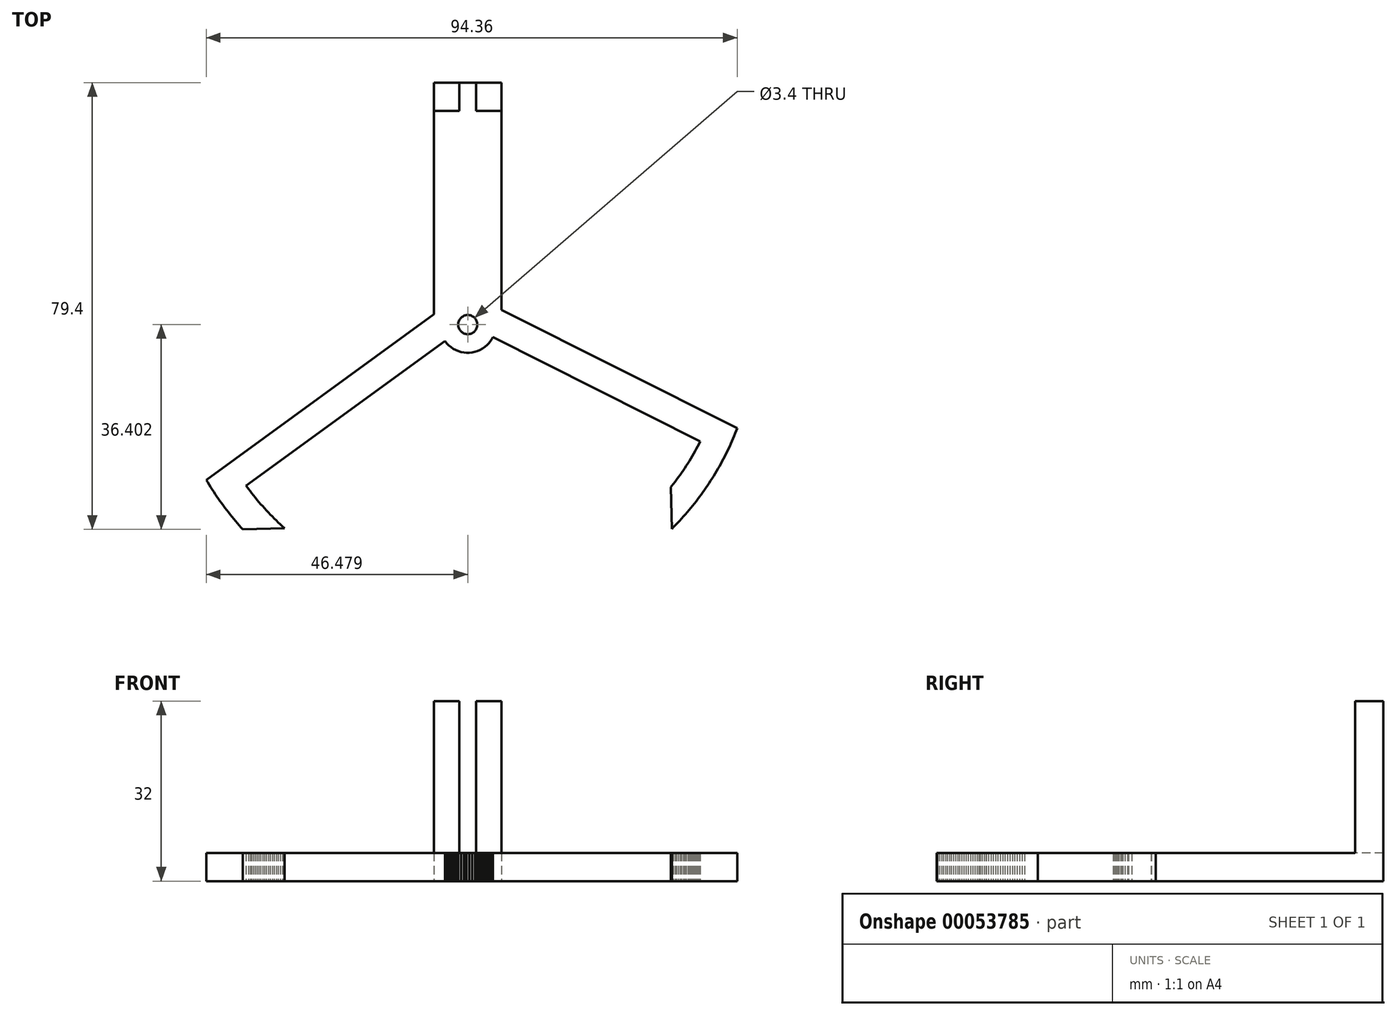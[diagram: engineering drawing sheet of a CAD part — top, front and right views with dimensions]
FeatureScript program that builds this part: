
annotation { "Feature Type Name" : "Feature", "Feature Type Description" : "" }
export const myFeature = defineFeature(function(context is Context, id is Id, definition is map)
    precondition{}
    {
        {
            var Q0;
            Q0=qCreatedBy(makeId("Top.planeOp"),FACE);
            var sketch = newSketch(context, id + "F0", { "sketchPlane" : qUnion([Q0])});
            skPoint(sketch, "E0", {"position": v(-0.7, 15.7) * mm});
            skLineSegment(sketch, "E1", {"start": v(0.8, 58.7) * mm, "end": v(0.8, 53.7) * mm});
            skLineSegment(sketch, "E2", {"start": v(-2.2, 58.7) * mm, "end": v(-2.2, 53.7) * mm});
            skLineSegment(sketch, "E3", {"start": v(-6.7, 58.7) * mm, "end": v(5.3, 58.7) * mm});
            skLineSegment(sketch, "E4", {"start": v(-6.7, 14.7) * mm, "end": v(-6.7, 58.7) * mm});
            skLineSegment(sketch, "E5", {"start": v(5.3, 14.7) * mm, "end": v(5.3, 58.7) * mm});
            skLineSegment(sketch, "E6", {"start": v(-6.7, 15.7) * mm, "end": v(5.3, 15.7) * mm, "construction": true});
            skLineSegment(sketch, "E7", {"start": v(-6.7, 14.7) * mm, "end": v(5.3, 14.7) * mm});
            skLineSegment(sketch, "E8", {"start": v(-6.7, 53.7) * mm, "end": v(5.3, 53.7) * mm});
            skLineSegment(sketch, "E9", {"start": v(-0.7, 14.7) * mm, "end": v(-0.7, 58.7) * mm, "construction": true});
            skCircle(sketch, "E10", {"center": v(-0.7, 15.7) * mm, "radius": 1.7 * mm});
            skPoint(sketch, "E9.startSnap0", {"position": v(-0.7, 14.7) * mm});
            skLineSegment(sketch, "E11", {"start": v(-33.28, -20.48) * mm, "end": v(-33.65, -20.15) * mm});
            skLineSegment(sketch, "E12", {"start": v(-33.65, -20.15) * mm, "end": v(-34.02, -19.8) * mm});
            skLineSegment(sketch, "E13", {"start": v(-34.02, -19.8) * mm, "end": v(-34.38, -19.46) * mm});
            skLineSegment(sketch, "E14", {"start": v(-34.38, -19.46) * mm, "end": v(-34.74, -19.11) * mm});
            skLineSegment(sketch, "E15", {"start": v(-34.74, -19.11) * mm, "end": v(-35.1, -18.76) * mm});
            skLineSegment(sketch, "E16", {"start": v(-35.1, -18.76) * mm, "end": v(-35.45, -18.4) * mm});
            skLineSegment(sketch, "E17", {"start": v(-35.45, -18.4) * mm, "end": v(-35.8, -18.05) * mm});
            skLineSegment(sketch, "E18", {"start": v(-35.8, -18.05) * mm, "end": v(-36.14, -17.69) * mm});
            skLineSegment(sketch, "E19", {"start": v(-36.14, -17.69) * mm, "end": v(-36.48, -17.32) * mm});
            skLineSegment(sketch, "E20", {"start": v(-36.48, -17.32) * mm, "end": v(-36.82, -16.95) * mm});
            skLineSegment(sketch, "E21", {"start": v(-36.82, -16.95) * mm, "end": v(-37.15, -16.58) * mm});
            skLineSegment(sketch, "E22", {"start": v(-37.15, -16.58) * mm, "end": v(-37.48, -16.2) * mm});
            skLineSegment(sketch, "E23", {"start": v(-37.48, -16.2) * mm, "end": v(-37.8, -15.82) * mm});
            skLineSegment(sketch, "E24", {"start": v(-37.8, -15.82) * mm, "end": v(-38.13, -15.44) * mm});
            skLineSegment(sketch, "E25", {"start": v(-38.13, -15.44) * mm, "end": v(-38.45, -15.06) * mm});
            skLineSegment(sketch, "E26", {"start": v(-38.45, -15.06) * mm, "end": v(-38.76, -14.67) * mm});
            skLineSegment(sketch, "E27", {"start": v(-38.76, -14.67) * mm, "end": v(-39.07, -14.27) * mm});
            skLineSegment(sketch, "E28", {"start": v(-39.07, -14.27) * mm, "end": v(-39.38, -13.88) * mm});
            skLineSegment(sketch, "E29", {"start": v(-39.38, -13.88) * mm, "end": v(-39.68, -13.48) * mm});
            skLineSegment(sketch, "E30", {"start": v(-39.68, -13.48) * mm, "end": v(-39.98, -13.08) * mm});
            skLineSegment(sketch, "E31", {"start": v(-39.98, -13.08) * mm, "end": v(-40.1, -12.92) * mm});
            skLineSegment(sketch, "E32", {"start": v(-40.1, -12.92) * mm, "end": v(-4.75, 12.76) * mm});
            skLineSegment(sketch, "E33", {"start": v(-4.75, 12.76) * mm, "end": v(-4.43, 12.37) * mm});
            skLineSegment(sketch, "E34", {"start": v(-4.43, 12.37) * mm, "end": v(-4.08, 12.02) * mm});
            skLineSegment(sketch, "E35", {"start": v(-4.08, 12.02) * mm, "end": v(-3.7, 11.7) * mm});
            skLineSegment(sketch, "E36", {"start": v(-3.7, 11.7) * mm, "end": v(-3.28, 11.42) * mm});
            skLineSegment(sketch, "E37", {"start": v(-3.28, 11.42) * mm, "end": v(-2.84, 11.18) * mm});
            skLineSegment(sketch, "E38", {"start": v(-2.84, 11.18) * mm, "end": v(-2.38, 11) * mm});
            skLineSegment(sketch, "E39", {"start": v(-2.38, 11) * mm, "end": v(-1.9, 10.85) * mm});
            skLineSegment(sketch, "E40", {"start": v(-1.9, 10.85) * mm, "end": v(-1.41, 10.75) * mm});
            skLineSegment(sketch, "E41", {"start": v(-1.41, 10.75) * mm, "end": v(-0.91, 10.7) * mm});
            skLineSegment(sketch, "E42", {"start": v(-0.91, 10.7) * mm, "end": v(-0.41, 10.71) * mm});
            skLineSegment(sketch, "E43", {"start": v(-0.41, 10.71) * mm, "end": v(0.08, 10.76) * mm});
            skLineSegment(sketch, "E44", {"start": v(0.08, 10.76) * mm, "end": v(0.57, 10.87) * mm});
            skLineSegment(sketch, "E45", {"start": v(0.57, 10.87) * mm, "end": v(1.05, 11.02) * mm});
            skLineSegment(sketch, "E46", {"start": v(1.05, 11.02) * mm, "end": v(1.5, 11.22) * mm});
            skLineSegment(sketch, "E47", {"start": v(1.5, 11.22) * mm, "end": v(1.94, 11.46) * mm});
            skLineSegment(sketch, "E48", {"start": v(1.94, 11.46) * mm, "end": v(2.35, 11.74) * mm});
            skLineSegment(sketch, "E49", {"start": v(2.35, 11.74) * mm, "end": v(2.73, 12.07) * mm});
            skLineSegment(sketch, "E50", {"start": v(2.73, 12.07) * mm, "end": v(3.08, 12.43) * mm});
            skLineSegment(sketch, "E51", {"start": v(3.08, 12.43) * mm, "end": v(3.39, 12.82) * mm});
            skLineSegment(sketch, "E52", {"start": v(3.39, 12.82) * mm, "end": v(3.65, 13.25) * mm});
            skLineSegment(sketch, "E53", {"start": v(3.65, 13.25) * mm, "end": v(3.77, 13.46) * mm});
            skLineSegment(sketch, "E54", {"start": v(3.77, 13.46) * mm, "end": v(40.61, -5.03) * mm});
            skLineSegment(sketch, "E55", {"start": v(40.61, -5.03) * mm, "end": v(40.39, -5.48) * mm});
            skLineSegment(sketch, "E56", {"start": v(40.39, -5.48) * mm, "end": v(40.15, -5.92) * mm});
            skLineSegment(sketch, "E57", {"start": v(40.15, -5.92) * mm, "end": v(39.92, -6.36) * mm});
            skLineSegment(sketch, "E58", {"start": v(39.92, -6.36) * mm, "end": v(39.68, -6.8) * mm});
            skLineSegment(sketch, "E59", {"start": v(39.68, -6.8) * mm, "end": v(39.43, -7.23) * mm});
            skLineSegment(sketch, "E60", {"start": v(39.43, -7.23) * mm, "end": v(39.18, -7.67) * mm});
            skLineSegment(sketch, "E61", {"start": v(39.18, -7.67) * mm, "end": v(38.93, -8.1) * mm});
            skLineSegment(sketch, "E62", {"start": v(38.93, -8.1) * mm, "end": v(38.67, -8.52) * mm});
            skLineSegment(sketch, "E63", {"start": v(38.67, -8.52) * mm, "end": v(38.4, -8.95) * mm});
            skLineSegment(sketch, "E64", {"start": v(38.4, -8.95) * mm, "end": v(38.13, -9.37) * mm});
            skLineSegment(sketch, "E65", {"start": v(38.13, -9.37) * mm, "end": v(37.86, -9.79) * mm});
            skLineSegment(sketch, "E66", {"start": v(37.86, -9.79) * mm, "end": v(37.58, -10.2) * mm});
            skLineSegment(sketch, "E67", {"start": v(37.58, -10.2) * mm, "end": v(37.3, -10.62) * mm});
            skLineSegment(sketch, "E68", {"start": v(37.3, -10.62) * mm, "end": v(37.01, -11.03) * mm});
            skLineSegment(sketch, "E69", {"start": v(37.01, -11.03) * mm, "end": v(36.72, -11.43) * mm});
            skLineSegment(sketch, "E70", {"start": v(36.72, -11.43) * mm, "end": v(36.42, -11.83) * mm});
            skLineSegment(sketch, "E71", {"start": v(36.42, -11.83) * mm, "end": v(36.12, -12.23) * mm});
            skLineSegment(sketch, "E72", {"start": v(36.12, -12.23) * mm, "end": v(35.82, -12.63) * mm});
            skLineSegment(sketch, "E73", {"start": v(35.82, -12.63) * mm, "end": v(35.51, -13.02) * mm});
            skLineSegment(sketch, "E74", {"start": v(35.51, -13.02) * mm, "end": v(35.4, -13.17) * mm});
            skLineSegment(sketch, "E75", {"start": v(35.4, -13.17) * mm, "end": v(35.57, -20.6) * mm});
            skLineSegment(sketch, "E76", {"start": v(35.57, -20.6) * mm, "end": v(35.92, -20.24) * mm});
            skLineSegment(sketch, "E77", {"start": v(35.92, -20.24) * mm, "end": v(36.27, -19.88) * mm});
            skLineSegment(sketch, "E78", {"start": v(36.27, -19.88) * mm, "end": v(36.61, -19.52) * mm});
            skLineSegment(sketch, "E79", {"start": v(36.61, -19.52) * mm, "end": v(36.95, -19.15) * mm});
            skLineSegment(sketch, "E80", {"start": v(36.95, -19.15) * mm, "end": v(37.3, -18.78) * mm});
            skLineSegment(sketch, "E81", {"start": v(37.3, -18.78) * mm, "end": v(37.63, -18.4) * mm});
            skLineSegment(sketch, "E82", {"start": v(37.63, -18.4) * mm, "end": v(37.96, -18.03) * mm});
            skLineSegment(sketch, "E83", {"start": v(37.96, -18.03) * mm, "end": v(38.28, -17.66) * mm});
            skLineSegment(sketch, "E84", {"start": v(38.28, -17.66) * mm, "end": v(38.6, -17.27) * mm});
            skLineSegment(sketch, "E85", {"start": v(38.6, -17.27) * mm, "end": v(38.93, -16.89) * mm});
            skLineSegment(sketch, "E86", {"start": v(38.93, -16.89) * mm, "end": v(39.24, -16.5) * mm});
            skLineSegment(sketch, "E87", {"start": v(39.24, -16.5) * mm, "end": v(39.55, -16.11) * mm});
            skLineSegment(sketch, "E88", {"start": v(39.55, -16.11) * mm, "end": v(39.86, -15.72) * mm});
            skLineSegment(sketch, "E89", {"start": v(39.86, -15.72) * mm, "end": v(40.17, -15.32) * mm});
            skLineSegment(sketch, "E90", {"start": v(40.17, -15.32) * mm, "end": v(40.47, -14.92) * mm});
            skLineSegment(sketch, "E91", {"start": v(40.47, -14.92) * mm, "end": v(40.76, -14.52) * mm});
            skLineSegment(sketch, "E92", {"start": v(40.76, -14.52) * mm, "end": v(41.06, -14.11) * mm});
            skLineSegment(sketch, "E93", {"start": v(41.06, -14.11) * mm, "end": v(41.34, -13.7) * mm});
            skLineSegment(sketch, "E94", {"start": v(41.34, -13.7) * mm, "end": v(41.63, -13.3) * mm});
            skLineSegment(sketch, "E95", {"start": v(41.63, -13.3) * mm, "end": v(41.9, -12.88) * mm});
            skLineSegment(sketch, "E96", {"start": v(41.9, -12.88) * mm, "end": v(42.19, -12.46) * mm});
            skLineSegment(sketch, "E97", {"start": v(42.19, -12.46) * mm, "end": v(42.46, -12.04) * mm});
            skLineSegment(sketch, "E98", {"start": v(42.46, -12.04) * mm, "end": v(42.73, -11.62) * mm});
            skLineSegment(sketch, "E99", {"start": v(42.73, -11.62) * mm, "end": v(43, -11.2) * mm});
            skLineSegment(sketch, "E100", {"start": v(43, -11.2) * mm, "end": v(43.25, -10.77) * mm});
            skLineSegment(sketch, "E101", {"start": v(43.25, -10.77) * mm, "end": v(43.5, -10.34) * mm});
            skLineSegment(sketch, "E102", {"start": v(43.5, -10.34) * mm, "end": v(43.76, -9.9) * mm});
            skLineSegment(sketch, "E103", {"start": v(43.76, -9.9) * mm, "end": v(44, -9.47) * mm});
            skLineSegment(sketch, "E104", {"start": v(44, -9.47) * mm, "end": v(44.25, -9.04) * mm});
            skLineSegment(sketch, "E105", {"start": v(44.25, -9.04) * mm, "end": v(44.49, -8.6) * mm});
            skLineSegment(sketch, "E106", {"start": v(44.49, -8.6) * mm, "end": v(44.72, -8.16) * mm});
            skLineSegment(sketch, "E107", {"start": v(44.72, -8.16) * mm, "end": v(44.95, -7.71) * mm});
            skLineSegment(sketch, "E108", {"start": v(44.95, -7.71) * mm, "end": v(45.18, -7.27) * mm});
            skLineSegment(sketch, "E109", {"start": v(45.18, -7.27) * mm, "end": v(45.4, -6.82) * mm});
            skLineSegment(sketch, "E110", {"start": v(45.4, -6.82) * mm, "end": v(45.62, -6.37) * mm});
            skLineSegment(sketch, "E111", {"start": v(45.62, -6.37) * mm, "end": v(45.83, -5.92) * mm});
            skLineSegment(sketch, "E112", {"start": v(45.83, -5.92) * mm, "end": v(46.04, -5.46) * mm});
            skLineSegment(sketch, "E113", {"start": v(46.04, -5.46) * mm, "end": v(46.24, -5) * mm});
            skLineSegment(sketch, "E114", {"start": v(46.24, -5) * mm, "end": v(46.44, -4.55) * mm});
            skLineSegment(sketch, "E115", {"start": v(46.44, -4.55) * mm, "end": v(46.64, -4.09) * mm});
            skLineSegment(sketch, "E116", {"start": v(46.64, -4.09) * mm, "end": v(46.83, -3.62) * mm});
            skLineSegment(sketch, "E117", {"start": v(46.83, -3.62) * mm, "end": v(47.01, -3.16) * mm});
            skLineSegment(sketch, "E118", {"start": v(47.01, -3.16) * mm, "end": v(47.18, -2.73) * mm});
            skLineSegment(sketch, "E119", {"start": v(47.18, -2.73) * mm, "end": v(1.54, 20.17) * mm});
            skLineSegment(sketch, "E120", {"start": v(1.54, 20.17) * mm, "end": v(1.08, 20.37) * mm});
            skLineSegment(sketch, "E121", {"start": v(1.08, 20.37) * mm, "end": v(0.6, 20.53) * mm});
            skLineSegment(sketch, "E122", {"start": v(0.6, 20.53) * mm, "end": v(0.12, 20.63) * mm});
            skLineSegment(sketch, "E123", {"start": v(0.12, 20.63) * mm, "end": v(-0.38, 20.7) * mm});
            skLineSegment(sketch, "E124", {"start": v(-0.38, 20.7) * mm, "end": v(-0.88, 20.7) * mm});
            skLineSegment(sketch, "E125", {"start": v(-0.88, 20.7) * mm, "end": v(-1.37, 20.66) * mm});
            skLineSegment(sketch, "E126", {"start": v(-1.37, 20.66) * mm, "end": v(-1.87, 20.56) * mm});
            skLineSegment(sketch, "E127", {"start": v(-1.87, 20.56) * mm, "end": v(-2.34, 20.42) * mm});
            skLineSegment(sketch, "E128", {"start": v(-2.34, 20.42) * mm, "end": v(-2.8, 20.24) * mm});
            skLineSegment(sketch, "E129", {"start": v(-2.8, 20.24) * mm, "end": v(-3.25, 20) * mm});
            skLineSegment(sketch, "E130", {"start": v(-3.25, 20) * mm, "end": v(-3.64, 19.75) * mm});
            skLineSegment(sketch, "E131", {"start": v(-3.64, 19.75) * mm, "end": v(-47.18, -11.89) * mm});
            skLineSegment(sketch, "E132", {"start": v(-47.18, -11.89) * mm, "end": v(-46.92, -12.32) * mm});
            skLineSegment(sketch, "E133", {"start": v(-46.92, -12.32) * mm, "end": v(-46.66, -12.74) * mm});
            skLineSegment(sketch, "E134", {"start": v(-46.66, -12.74) * mm, "end": v(-46.4, -13.17) * mm});
            skLineSegment(sketch, "E135", {"start": v(-46.4, -13.17) * mm, "end": v(-46.13, -13.59) * mm});
            skLineSegment(sketch, "E136", {"start": v(-46.13, -13.59) * mm, "end": v(-45.86, -14) * mm});
            skLineSegment(sketch, "E137", {"start": v(-45.86, -14) * mm, "end": v(-45.58, -14.42) * mm});
            skLineSegment(sketch, "E138", {"start": v(-45.58, -14.42) * mm, "end": v(-45.3, -14.84) * mm});
            skLineSegment(sketch, "E139", {"start": v(-45.3, -14.84) * mm, "end": v(-45.01, -15.25) * mm});
            skLineSegment(sketch, "E140", {"start": v(-45.01, -15.25) * mm, "end": v(-44.73, -15.66) * mm});
            skLineSegment(sketch, "E141", {"start": v(-44.73, -15.66) * mm, "end": v(-44.43, -16.06) * mm});
            skLineSegment(sketch, "E142", {"start": v(-44.43, -16.06) * mm, "end": v(-44.14, -16.47) * mm});
            skLineSegment(sketch, "E143", {"start": v(-44.14, -16.47) * mm, "end": v(-43.84, -16.87) * mm});
            skLineSegment(sketch, "E144", {"start": v(-43.84, -16.87) * mm, "end": v(-43.54, -17.26) * mm});
            skLineSegment(sketch, "E145", {"start": v(-43.54, -17.26) * mm, "end": v(-43.23, -17.66) * mm});
            skLineSegment(sketch, "E146", {"start": v(-43.23, -17.66) * mm, "end": v(-42.92, -18.05) * mm});
            skLineSegment(sketch, "E147", {"start": v(-42.92, -18.05) * mm, "end": v(-42.6, -18.44) * mm});
            skLineSegment(sketch, "E148", {"start": v(-42.6, -18.44) * mm, "end": v(-42.29, -18.83) * mm});
            skLineSegment(sketch, "E149", {"start": v(-42.29, -18.83) * mm, "end": v(-41.97, -19.2) * mm});
            skLineSegment(sketch, "E150", {"start": v(-41.97, -19.2) * mm, "end": v(-41.64, -19.59) * mm});
            skLineSegment(sketch, "E151", {"start": v(-41.64, -19.59) * mm, "end": v(-41.31, -19.97) * mm});
            skLineSegment(sketch, "E152", {"start": v(-41.31, -19.97) * mm, "end": v(-40.98, -20.34) * mm});
            skLineSegment(sketch, "E153", {"start": v(-40.98, -20.34) * mm, "end": v(-40.66, -20.7) * mm});
            skLineSegment(sketch, "E154", {"start": v(-40.66, -20.7) * mm, "end": v(-33.28, -20.48) * mm});
            skSolve(sketch);
        }
        {
            var Q0;
            Q0=makeQuery(id+"F0.imprint","IMPRINT",FACE,{"disambiguationData":[TD([[makeQuery(id+"F0.imprint","IMPRINT",EDGE,{"derivedFrom":sQuery(id+"F0.wireOp",EDGE,"E11")}),1.0]])]});
            var Q1;
            {var subQ0=sQuery(id+"F0.wireOp",EDGE,"E120");Q1=makeQuery(id+"F0.imprint","IMPRINT",FACE,{"disambiguationData":[TD([[makeQuery(id+"F0.imprint","IMPRINT",EDGE,{"derivedFrom":subQ0}),1.0]])]});}
            var Q2;
            {var subQ0=sQuery(id+"F0.wireOp",EDGE,"E120");Q2=makeQuery(id+"F0.imprint","IMPRINT",FACE,{"disambiguationData":[TD([[makeQuery(id+"F0.imprint","IMPRINT",EDGE,{"derivedFrom":subQ0}),-1.0]])]});}
            var Q3;
            {var subQ0=sQuery(id+"F0.wireOp",EDGE,"E1");Q3=makeQuery(id+"F0.imprint","IMPRINT",FACE,{"disambiguationData":[TD([[makeQuery(id+"F0.imprint","IMPRINT",EDGE,{"derivedFrom":subQ0}),-1.0]])]});}
            extrude(context, id + "F1", {"entities" : qUnion([Q0, Q1, Q2, Q3]), "depth" : 5 * mm});
        }
        {
            var Q0;
            {var subQ0=sQuery(id+"F0.wireOp",EDGE,"E2");Q0=makeQuery(id+"F0.imprint","IMPRINT",FACE,{"disambiguationData":[TD([[makeQuery(id+"F0.imprint","IMPRINT",EDGE,{"derivedFrom":subQ0}),-1.0]])]});}
            var Q1;
            {var subQ0=sQuery(id+"F0.wireOp",EDGE,"E1");Q1=makeQuery(id+"F0.imprint","IMPRINT",FACE,{"disambiguationData":[TD([[makeQuery(id+"F0.imprint","IMPRINT",EDGE,{"derivedFrom":subQ0}),1.0]])]});}
            extrude(context, id + "F2", {"entities" : qUnion([Q0, Q1]), "operationType" : NewBodyOperationType.ADD, "depth" : (27 + 5) * mm});
        }
    });
